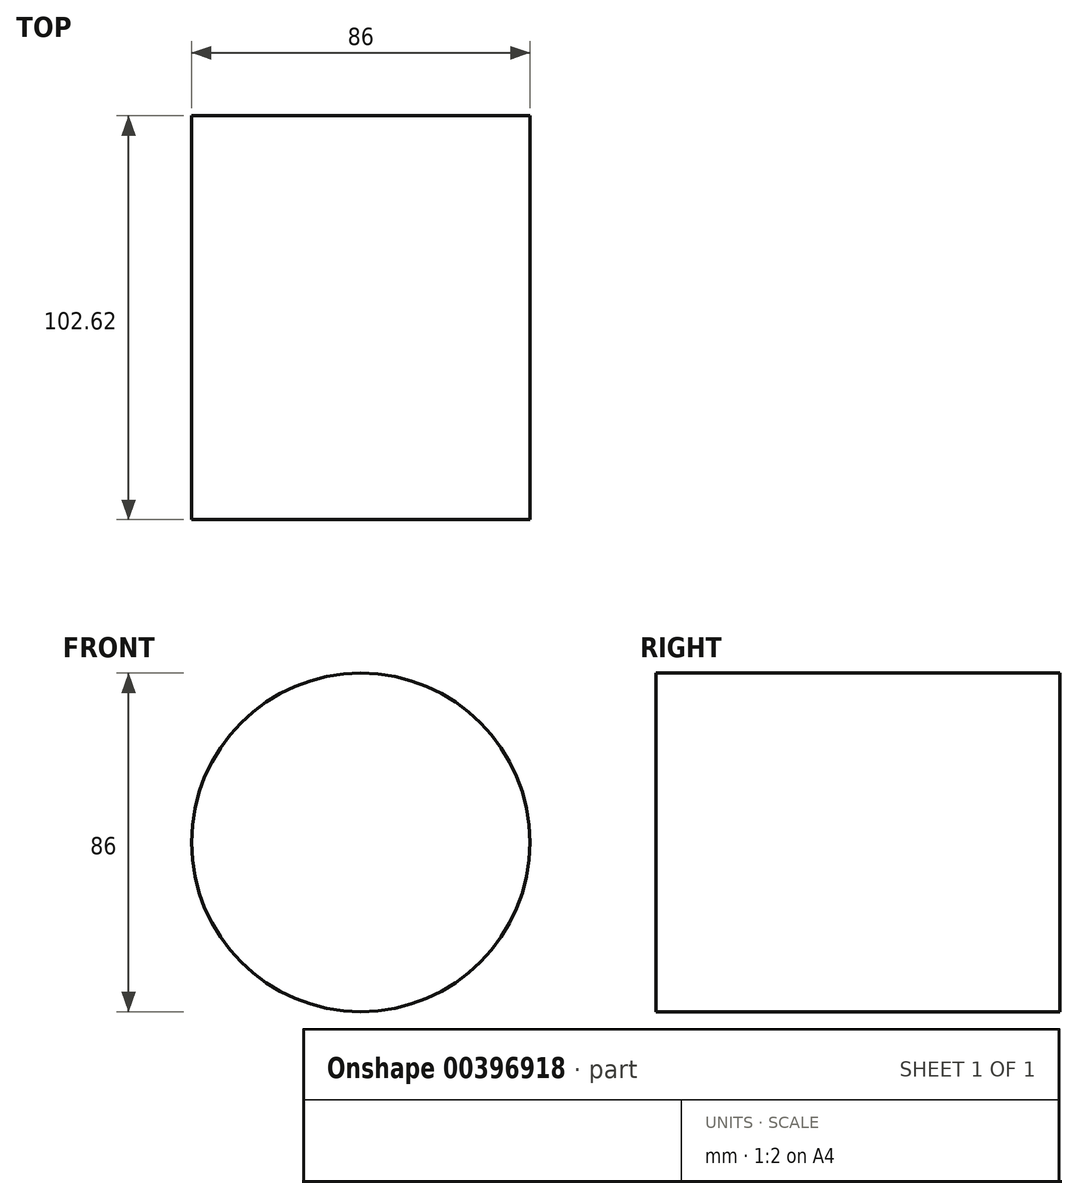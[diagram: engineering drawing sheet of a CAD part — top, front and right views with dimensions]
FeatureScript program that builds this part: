
annotation { "Feature Type Name" : "Feature", "Feature Type Description" : "" }
export const myFeature = defineFeature(function(context is Context, id is Id, definition is map)
    precondition{}
    {
        {
            var Q0;
            Q0=qCreatedBy(makeId("Front.planeOp"),FACE);
            var sketch = newSketch(context, id + "F0", { "sketchPlane" : qUnion([Q0])});
            skCircle(sketch, "E0", {"center": v(0, 0) * mm, "radius": 37.67 * mm});
            skSolve(sketch);
        }
        {
            var Q0;
            Q0=makeQuery(id+"F0.imprint","IMPRINT",FACE,{"disambiguationData":[TD([[makeQuery(id+"F0.imprint","IMPRINT",EDGE,{"derivedFrom":sQuery(id+"F0.wireOp",EDGE,"E0")}),1.0]])]});
            extrude(context, id + "F1", {"entities" : qUnion([Q0]), "depth" : 101.6 * mm, "hasDraft" : true, "draftAngle" : 3 * degree});
        }
        {
            var Q0;
            Q0=makeQuery(id+"F1.opExtrude","CAP_FACE",FACE,{"disambiguationData":[OSD([sQuery(id+"F0.wireOp",EDGE,"E0")])],"isStart":false});
            extrude(context, id + "F2", {"entities" : qUnion([Q0]), "operationType" : NewBodyOperationType.ADD, "oppositeDirection" : true, "depth" : 102.62 * mm});
        }
    });
